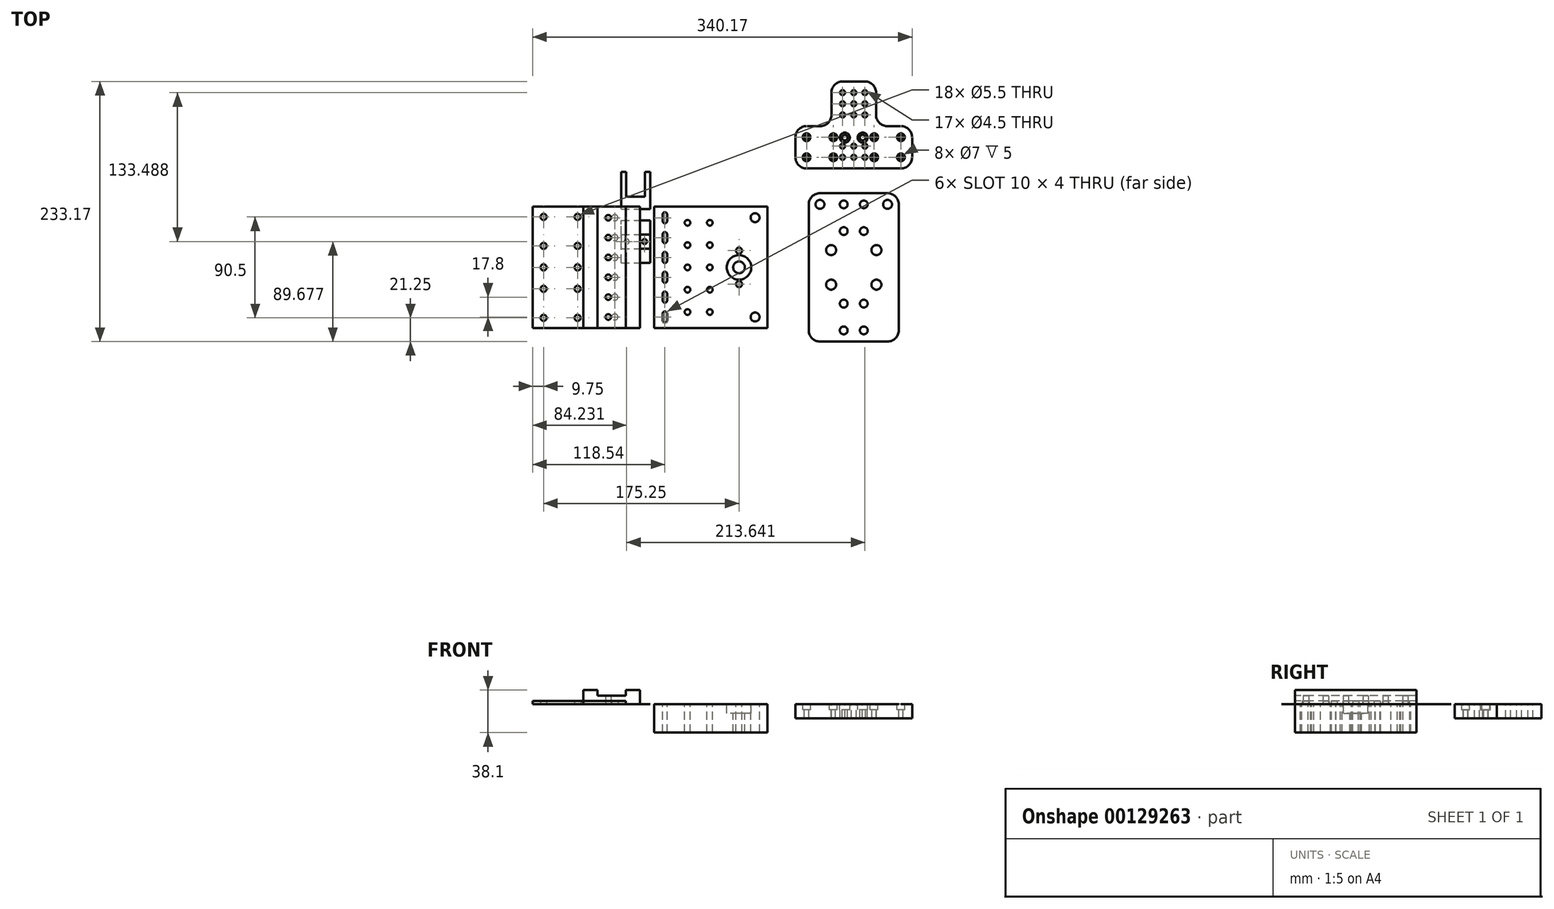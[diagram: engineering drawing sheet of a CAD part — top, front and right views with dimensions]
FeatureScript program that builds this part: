
annotation { "Feature Type Name" : "Feature", "Feature Type Description" : "" }
export const myFeature = defineFeature(function(context is Context, id is Id, definition is map)
    precondition{}
    {
        {
            var Q0;
            Q0=qCreatedBy(makeId("Top.planeOp"),FACE);
            var sketch = newSketch(context, id + "F0", { "sketchPlane" : qUnion([Q0])});
            skLineSegment(sketch, "E0.bottom", {"start": v(0, 0) * mm, "end": v(101.6, 0) * mm});
            skLineSegment(sketch, "E0.top", {"start": v(0, 109) * mm, "end": v(101.6, 109) * mm});
            skLineSegment(sketch, "E0.left", {"start": v(0, 0) * mm, "end": v(0, 109) * mm});
            skLineSegment(sketch, "E0.right", {"start": v(101.6, 0) * mm, "end": v(101.6, 109) * mm});
            skLineSegment(sketch, "E1", {"start": v(9.74, 0) * mm, "end": v(9.74, 109) * mm, "construction": true});
            skLineSegment(sketch, "E2", {"start": v(0, 10) * mm, "end": v(9.74, 10) * mm, "construction": true});
            skLineSegment(sketch, "E3.0.1.0", {"start": v(0, 27.8) * mm, "end": v(9.74, 27.8) * mm, "construction": true});
            skLineSegment(sketch, "E3.0.2.0", {"start": v(0, 45.6) * mm, "end": v(9.74, 45.6) * mm, "construction": true});
            skLineSegment(sketch, "E3.0.3.0", {"start": v(0, 63.4) * mm, "end": v(9.74, 63.4) * mm, "construction": true});
            skLineSegment(sketch, "E3.0.4.0", {"start": v(0, 81.2) * mm, "end": v(9.74, 81.2) * mm, "construction": true});
            skLineSegment(sketch, "E3.0.5.0", {"start": v(0, 99) * mm, "end": v(9.74, 99) * mm, "construction": true});
            skLineSegment(sketch, "E3.direction2", {"start": v(0, 10) * mm, "end": v(0, 27.8) * mm, "construction": true});
            skArc(sketch, "E4", {"start": v(11.74, 30.8) * mm, "mid": v(9.74, 32.8) * mm, "end": v(7.74, 30.8) * mm});
            skLineSegment(sketch, "E5", {"start": v(9.74, 30.8) * mm, "end": v(9.74, 24.8) * mm, "construction": true});
            skArc(sketch, "E6", {"start": v(7.74, 24.8) * mm, "mid": v(9.74, 22.8) * mm, "end": v(11.74, 24.8) * mm});
            skLineSegment(sketch, "E7", {"start": v(11.74, 30.8) * mm, "end": v(11.74, 24.8) * mm});
            skLineSegment(sketch, "E8", {"start": v(7.74, 24.8) * mm, "end": v(7.74, 30.8) * mm});
            skPoint(sketch, "E9", {"position": v(9.74, 27.8) * mm});
            skArc(sketch, "E10", {"start": v(11.74, 48.6) * mm, "mid": v(9.74, 50.6) * mm, "end": v(7.74, 48.6) * mm});
            skLineSegment(sketch, "E11", {"start": v(9.74, 48.6) * mm, "end": v(9.74, 42.6) * mm, "construction": true});
            skArc(sketch, "E12", {"start": v(7.74, 42.6) * mm, "mid": v(9.74, 40.6) * mm, "end": v(11.74, 42.6) * mm});
            skLineSegment(sketch, "E13", {"start": v(11.74, 48.6) * mm, "end": v(11.74, 42.6) * mm});
            skLineSegment(sketch, "E14", {"start": v(7.74, 42.6) * mm, "end": v(7.74, 48.6) * mm});
            skPoint(sketch, "E15", {"position": v(9.74, 45.6) * mm});
            skArc(sketch, "E16", {"start": v(11.74, 102) * mm, "mid": v(9.74, 104) * mm, "end": v(7.74, 102) * mm});
            skLineSegment(sketch, "E17", {"start": v(9.74, 102) * mm, "end": v(9.74, 96) * mm, "construction": true});
            skArc(sketch, "E18", {"start": v(7.74, 96) * mm, "mid": v(9.74, 94) * mm, "end": v(11.74, 96) * mm});
            skLineSegment(sketch, "E19", {"start": v(11.74, 102) * mm, "end": v(11.74, 96) * mm});
            skLineSegment(sketch, "E20", {"start": v(7.74, 96) * mm, "end": v(7.74, 102) * mm});
            skPoint(sketch, "E21", {"position": v(9.74, 99) * mm});
            skArc(sketch, "E22", {"start": v(11.74, 13) * mm, "mid": v(9.74, 15) * mm, "end": v(7.74, 13) * mm});
            skLineSegment(sketch, "E23", {"start": v(9.74, 13) * mm, "end": v(9.74, 7) * mm, "construction": true});
            skArc(sketch, "E24", {"start": v(7.74, 7) * mm, "mid": v(9.74, 5) * mm, "end": v(11.74, 7) * mm});
            skLineSegment(sketch, "E25", {"start": v(11.74, 13) * mm, "end": v(11.74, 7) * mm});
            skLineSegment(sketch, "E26", {"start": v(7.74, 7) * mm, "end": v(7.74, 13) * mm});
            skPoint(sketch, "E27", {"position": v(9.74, 10) * mm});
            skArc(sketch, "E28", {"start": v(11.74, 84.2) * mm, "mid": v(9.74, 86.2) * mm, "end": v(7.74, 84.2) * mm});
            skLineSegment(sketch, "E29", {"start": v(9.74, 84.2) * mm, "end": v(9.74, 78.2) * mm, "construction": true});
            skArc(sketch, "E30", {"start": v(7.74, 78.2) * mm, "mid": v(9.74, 76.2) * mm, "end": v(11.74, 78.2) * mm});
            skLineSegment(sketch, "E31", {"start": v(11.74, 84.2) * mm, "end": v(11.74, 78.2) * mm});
            skLineSegment(sketch, "E32", {"start": v(7.74, 78.2) * mm, "end": v(7.74, 84.2) * mm});
            skPoint(sketch, "E33", {"position": v(9.74, 81.2) * mm});
            skArc(sketch, "E34", {"start": v(11.74, 66.4) * mm, "mid": v(9.74, 68.4) * mm, "end": v(7.74, 66.4) * mm});
            skLineSegment(sketch, "E35", {"start": v(9.74, 66.4) * mm, "end": v(9.74, 60.4) * mm, "construction": true});
            skArc(sketch, "E36", {"start": v(7.74, 60.4) * mm, "mid": v(9.74, 58.4) * mm, "end": v(11.74, 60.4) * mm});
            skLineSegment(sketch, "E37", {"start": v(11.74, 66.4) * mm, "end": v(11.74, 60.4) * mm});
            skLineSegment(sketch, "E38", {"start": v(7.74, 60.4) * mm, "end": v(7.74, 66.4) * mm});
            skPoint(sketch, "E39", {"position": v(9.74, 63.4) * mm});
            skLineSegment(sketch, "E40", {"start": v(76.2, 109) * mm, "end": v(76.2, 0) * mm, "construction": true});
            skPoint(sketch, "E41", {"position": v(76.2, 69.5) * mm});
            skPoint(sketch, "E42", {"position": v(76.2, 54.5) * mm});
            skPoint(sketch, "E43", {"position": v(76.2, 39.5) * mm});
            skCircle(sketch, "E44", {"center": v(76.2, 69.5) * mm, "radius": 2.75 * mm});
            skCircle(sketch, "E45", {"center": v(76.2, 39.5) * mm, "radius": 2.75 * mm});
            skCircle(sketch, "E46", {"center": v(76.2, 54.5) * mm, "radius": 11 * mm});
            skCircle(sketch, "E47", {"center": v(76.2, 54.5) * mm, "radius": 5.26 * mm});
            skLineSegment(sketch, "E48", {"start": v(122.66, 27) * mm, "end": v(122.66, -7) * mm, "construction": true});
            skLineSegment(sketch, "E49", {"start": v(90.6, 10) * mm, "end": v(122.66, 10) * mm, "construction": true});
            skPoint(sketch, "E50", {"position": v(122.66, 10) * mm});
            skLineSegment(sketch, "E51", {"start": v(90.6, 99) * mm, "end": v(122.66, 99) * mm, "construction": true});
            skLineSegment(sketch, "E52", {"start": v(122.66, 116) * mm, "end": v(122.66, 82) * mm, "construction": true});
            skPoint(sketch, "E53", {"position": v(122.66, 99) * mm});
            skLineSegment(sketch, "E54", {"start": v(122.66, 54.5) * mm, "end": v(76.2, 54.5) * mm, "construction": true});
            skLineSegment(sketch, "E55", {"start": v(122.66, 74.5) * mm, "end": v(122.66, 34.5) * mm, "construction": true});
            skPoint(sketch, "E56", {"position": v(122.66, 54.5) * mm});
            skLineSegment(sketch, "E57", {"start": v(90.6, 109) * mm, "end": v(90.6, 0) * mm, "construction": true});
            skPoint(sketch, "E58", {"position": v(90.6, 99) * mm});
            skPoint(sketch, "E59", {"position": v(90.6, 10) * mm});
            skLineSegment(sketch, "E60", {"start": v(122.66, 82) * mm, "end": v(122.66, 74.5) * mm, "construction": true});
            skLineSegment(sketch, "E61", {"start": v(122.66, 34.5) * mm, "end": v(122.66, 27) * mm, "construction": true});
            skCircle(sketch, "E62", {"center": v(90.6, 99) * mm, "radius": 4 * mm});
            skCircle(sketch, "E63", {"center": v(90.6, 10) * mm, "radius": 4 * mm});
            skLineSegment(sketch, "E64", {"start": v(30, 109) * mm, "end": v(30, 0) * mm, "construction": true});
            skLineSegment(sketch, "E65", {"start": v(50, 109) * mm, "end": v(50, 0) * mm, "construction": true});
            skLineSegment(sketch, "E66", {"start": v(50, 54.5) * mm, "end": v(30, 54.5) * mm, "construction": true});
            skLineSegment(sketch, "E67", {"start": v(30, 74.5) * mm, "end": v(50, 74.5) * mm, "construction": true});
            skLineSegment(sketch, "E68", {"start": v(50, 94.5) * mm, "end": v(30, 94.5) * mm, "construction": true});
            skLineSegment(sketch, "E69", {"start": v(30, 34.5) * mm, "end": v(50, 34.5) * mm, "construction": true});
            skLineSegment(sketch, "E70", {"start": v(50, 14.5) * mm, "end": v(30, 14.5) * mm, "construction": true});
            skCircle(sketch, "E71", {"center": v(30, 94.5) * mm, "radius": 2.55 * mm});
            skCircle(sketch, "E72", {"center": v(50, 94.5) * mm, "radius": 2.55 * mm});
            skCircle(sketch, "E73", {"center": v(30, 74.5) * mm, "radius": 2.55 * mm});
            skCircle(sketch, "E74", {"center": v(50, 74.5) * mm, "radius": 2.55 * mm});
            skCircle(sketch, "E75", {"center": v(50, 54.5) * mm, "radius": 2.55 * mm});
            skCircle(sketch, "E76", {"center": v(30, 54.5) * mm, "radius": 2.55 * mm});
            skCircle(sketch, "E77", {"center": v(30, 34.5) * mm, "radius": 2.55 * mm});
            skCircle(sketch, "E78", {"center": v(50, 34.5) * mm, "radius": 2.55 * mm});
            skCircle(sketch, "E79", {"center": v(50, 14.5) * mm, "radius": 2.55 * mm});
            skCircle(sketch, "E80", {"center": v(30, 14.5) * mm, "radius": 2.55 * mm});
            skLineSegment(sketch, "E81", {"start": v(101.6, 116.15) * mm, "end": v(101.6, 102.86) * mm});
            skLineSegment(sketch, "E82", {"start": v(76.2, 85.11) * mm, "end": v(94.2, 85.11) * mm});
            skSolve(sketch);
        }
        {
            var Q0;
            Q0=qCreatedBy(makeId("Top.planeOp"),FACE);
            var sketch = newSketch(context, id + "F1", { "sketchPlane" : qUnion([Q0])});
            skLineSegment(sketch, "E83.bottom", {"start": v(-25.4, 0) * mm, "end": v(-50.8, 0) * mm});
            skLineSegment(sketch, "E83.top", {"start": v(-25.4, 109) * mm, "end": v(-50.8, 109) * mm});
            skLineSegment(sketch, "E83.left", {"start": v(-25.4, 0) * mm, "end": v(-25.4, 109) * mm, "construction": true});
            skLineSegment(sketch, "E83.right", {"start": v(-50.8, 0) * mm, "end": v(-50.8, 109) * mm, "construction": true});
            skLineSegment(sketch, "E84", {"start": v(0, 0) * mm, "end": v(-25.4, 0) * mm, "construction": true});
            skLineSegment(sketch, "E85", {"start": v(-25.4, 109) * mm, "end": v(0, 109) * mm, "construction": true});
            skLineSegment(sketch, "E86", {"start": v(-50.8, 99) * mm, "end": v(0, 99) * mm, "construction": true});
            skLineSegment(sketch, "E87", {"start": v(-50.8, 81.2) * mm, "end": v(0, 81.2) * mm, "construction": true});
            skLineSegment(sketch, "E88", {"start": v(-50.8, 63.4) * mm, "end": v(0, 63.4) * mm, "construction": true});
            skLineSegment(sketch, "E89", {"start": v(-50.8, 45.6) * mm, "end": v(0, 45.6) * mm, "construction": true});
            skLineSegment(sketch, "E90", {"start": v(-50.8, 27.8) * mm, "end": v(0, 27.8) * mm, "construction": true});
            skLineSegment(sketch, "E91", {"start": v(-50.8, 10) * mm, "end": v(0, 10) * mm, "construction": true});
            skLineSegment(sketch, "E92", {"start": v(-41.06, 109) * mm, "end": v(-41.06, 0) * mm, "construction": true});
            skCircle(sketch, "E93", {"center": v(-41.06, 99) * mm, "radius": 2.5 * mm});
            skCircle(sketch, "E94", {"center": v(-41.06, 81.2) * mm, "radius": 2.5 * mm});
            skCircle(sketch, "E95", {"center": v(-41.06, 63.4) * mm, "radius": 2.5 * mm});
            skCircle(sketch, "E96", {"center": v(-41.06, 45.6) * mm, "radius": 2.5 * mm});
            skCircle(sketch, "E97", {"center": v(-41.06, 27.8) * mm, "radius": 2.5 * mm});
            skCircle(sketch, "E98", {"center": v(-41.06, 10) * mm, "radius": 2.5 * mm});
            skLineSegment(sketch, "E99", {"start": v(-50.8, 109) * mm, "end": v(-63.5, 109) * mm});
            skLineSegment(sketch, "E100", {"start": v(-63.5, 109) * mm, "end": v(-63.5, 0) * mm});
            skLineSegment(sketch, "E101", {"start": v(-63.5, 0) * mm, "end": v(-50.8, 0) * mm});
            skLineSegment(sketch, "E102", {"start": v(-25.4, 0) * mm, "end": v(-12.7, 0) * mm});
            skPoint(sketch, "E102.endSnap0", {"position": v(-12.7, 0) * mm});
            skLineSegment(sketch, "E103", {"start": v(-12.7, 0) * mm, "end": v(-12.7, 109) * mm});
            skLineSegment(sketch, "E104", {"start": v(-12.7, 109) * mm, "end": v(-25.4, 109) * mm});
            skSolve(sketch);
        }
        {
            var Q0;
            Q0=makeQuery(id+"F1.imprint","IMPRINT",FACE,{"disambiguationData":[TD([[makeQuery(id+"F1.imprint","IMPRINT",EDGE,{"derivedFrom":sQuery(id+"F1.wireOp",EDGE,"E83.bottom")}),-1.0]])]});
            extrude(context, id + "F2", {"entities" : qUnion([Q0]), "depth" : 12.7 * mm});
        }
        {
            var Q0;
            Q0=makeQuery(id+"F2.opExtrude","CAP_FACE",FACE,{"disambiguationData":[OSD([sQuery(id+"F1.wireOp",EDGE,"E83.bottom"),sQuery(id+"F1.wireOp",EDGE,"E83.top"),sQuery(id+"F1.wireOp",EDGE,"E93"),sQuery(id+"F1.wireOp",EDGE,"E94"),sQuery(id+"F1.wireOp",EDGE,"E95"),sQuery(id+"F1.wireOp",EDGE,"E96"),sQuery(id+"F1.wireOp",EDGE,"E97"),sQuery(id+"F1.wireOp",EDGE,"E98"),sQuery(id+"F1.wireOp",EDGE,"E99"),sQuery(id+"F1.wireOp",EDGE,"E100"),sQuery(id+"F1.wireOp",EDGE,"E101"),sQuery(id+"F1.wireOp",EDGE,"E102"),sQuery(id+"F1.wireOp",EDGE,"E103"),sQuery(id+"F1.wireOp",EDGE,"E104")])],"isStart":false});
            var sketch = newSketch(context, id + "F3", { "sketchPlane" : qUnion([Q0])});
            skLineSegment(sketch, "E105", {"start": v(-50.8, 109) * mm, "end": v(-50.8, 0) * mm});
            skLineSegment(sketch, "E106", {"start": v(-25.4, 109) * mm, "end": v(-25.4, 0) * mm});
            skSolve(sketch);
        }
        {
            var Q0;
            {var subQ0=sQuery(id+"F3.wireOp",EDGE,"E105");Q0=makeQuery(id+"F3.imprint","IMPRINT",FACE,{"disambiguationData":[TD([[makeQuery(id+"F3.imprint","IMPRINT",EDGE,{"derivedFrom":subQ0}),1.0]])]});}
            extrude(context, id + "F4", {"entities" : qUnion([Q0]), "operationType" : NewBodyOperationType.REMOVE, "oppositeDirection" : true, "depth" : 5 * mm});
        }
        {
            var Q0;
            Q0=makeQuery(id+"F0.imprint","IMPRINT",FACE,{"disambiguationData":[TD([[makeQuery(id+"F0.imprint","IMPRINT",EDGE,{"derivedFrom":sQuery(id+"F0.wireOp",EDGE,"E46")}),1.0]])]});
            var Q1;
            Q1=makeQuery(id+"F0.imprint","IMPRINT",FACE,{"disambiguationData":[TD([[makeQuery(id+"F0.imprint","IMPRINT",EDGE,{"derivedFrom":sQuery(id+"F0.wireOp",EDGE,"E0.bottom")}),1.0]])]});
            extrude(context, id + "F5", {"entities" : qUnion([Q0, Q1]), "oppositeDirection" : true, "depth" : 25.4 * mm});
        }
        {
            var Q0;
            Q0=makeQuery(id+"F0.imprint","IMPRINT",FACE,{"disambiguationData":[TD([[makeQuery(id+"F0.imprint","IMPRINT",EDGE,{"derivedFrom":sQuery(id+"F0.wireOp",EDGE,"E46")}),1.0]])]});
            extrude(context, id + "F6", {"entities" : qUnion([Q0]), "operationType" : NewBodyOperationType.REMOVE, "oppositeDirection" : true, "depth" : 8 * mm});
        }
        {
            var Q0;
            Q0=makeQuery(id+"F0.imprint","IMPRINT",FACE,{"disambiguationData":[TD([[makeQuery(id+"F0.imprint","IMPRINT",EDGE,{"derivedFrom":sQuery(id+"F0.wireOp",EDGE,"E0.bottom")}),1.0]])]});
            var sketch = newSketch(context, id + "F7", { "sketchPlane" : qUnion([Q0])});
            skLineSegment(sketch, "E107.bottom", {"start": v(-25.4, 109) * mm, "end": v(-58.8, 109) * mm});
            skLineSegment(sketch, "E107.top", {"start": v(-25.4, 0) * mm, "end": v(-108.8, 0) * mm});
            skLineSegment(sketch, "E107.left", {"start": v(-25.4, 109) * mm, "end": v(-25.4, 0) * mm});
            skLineSegment(sketch, "E107.right", {"start": v(-108.8, 109) * mm, "end": v(-108.8, 0) * mm});
            skLineSegment(sketch, "E108", {"start": v(0, 109) * mm, "end": v(-25.4, 109) * mm, "construction": true});
            skLineSegment(sketch, "E109", {"start": v(0, 0) * mm, "end": v(-25.4, 0) * mm, "construction": true});
            skLineSegment(sketch, "E110", {"start": v(-58.8, 109) * mm, "end": v(-58.8, 54.5) * mm, "construction": true});
            skLineSegment(sketch, "E111", {"start": v(-35.14, 109) * mm, "end": v(-35.14, 0) * mm, "construction": true});
            skLineSegment(sketch, "E112", {"start": v(-35.14, 99) * mm, "end": v(0, 99) * mm, "construction": true});
            skLineSegment(sketch, "E113", {"start": v(-35.14, 81.2) * mm, "end": v(0, 81.2) * mm, "construction": true});
            skLineSegment(sketch, "E114", {"start": v(-35.14, 63.4) * mm, "end": v(0, 63.4) * mm, "construction": true});
            skLineSegment(sketch, "E115", {"start": v(-35.14, 45.6) * mm, "end": v(0, 45.6) * mm, "construction": true});
            skLineSegment(sketch, "E116", {"start": v(-35.14, 27.8) * mm, "end": v(0, 27.8) * mm, "construction": true});
            skLineSegment(sketch, "E117", {"start": v(-35.14, 10) * mm, "end": v(0, 10) * mm, "construction": true});
            skPoint(sketch, "E118", {"position": v(9.74, 109) * mm});
            skLineSegment(sketch, "E119", {"start": v(0, 109) * mm, "end": v(9.74, 109) * mm, "construction": true});
            skLineSegment(sketch, "E120", {"start": v(-25.4, 109) * mm, "end": v(-35.14, 109) * mm, "construction": true});
            skCircle(sketch, "E121", {"center": v(-35.14, 99) * mm, "radius": 2.75 * mm});
            skCircle(sketch, "E122", {"center": v(-35.14, 81.2) * mm, "radius": 2.75 * mm});
            skCircle(sketch, "E123", {"center": v(-35.14, 63.4) * mm, "radius": 2.75 * mm});
            skCircle(sketch, "E124", {"center": v(-35.14, 45.6) * mm, "radius": 2.75 * mm});
            skCircle(sketch, "E125", {"center": v(-35.14, 27.8) * mm, "radius": 2.75 * mm});
            skCircle(sketch, "E126", {"center": v(-35.14, 10) * mm, "radius": 2.75 * mm});
            skLineSegment(sketch, "E127", {"start": v(-58.8, 54.5) * mm, "end": v(-108.8, 54.5) * mm, "construction": true});
            skLineSegment(sketch, "E128", {"start": v(-58.8, 109) * mm, "end": v(-83.8, 109) * mm});
            skLineSegment(sketch, "E129", {"start": v(-58.8, 54.5) * mm, "end": v(-58.8, 0) * mm, "construction": true});
            skLineSegment(sketch, "E130", {"start": v(-83.8, 109) * mm, "end": v(-83.8, 0) * mm, "construction": true});
            skLineSegment(sketch, "E131", {"start": v(-99.05, 109) * mm, "end": v(-99.05, 0) * mm, "construction": true});
            skLineSegment(sketch, "E132", {"start": v(-68.55, 109) * mm, "end": v(-68.55, 0) * mm, "construction": true});
            skLineSegment(sketch, "E133", {"start": v(-83.8, 109) * mm, "end": v(-108.8, 109) * mm});
            skLineSegment(sketch, "E134", {"start": v(-50.8, 109) * mm, "end": v(-50.8, 0) * mm, "construction": true});
            skLineSegment(sketch, "E135", {"start": v(-108.8, 64.5) * mm, "end": v(-58.8, 64.5) * mm, "construction": true});
            skLineSegment(sketch, "E136", {"start": v(-108.8, 44.5) * mm, "end": v(-58.8, 44.5) * mm, "construction": true});
            skLineSegment(sketch, "E137", {"start": v(-108.8, 86.75) * mm, "end": v(-58.8, 86.75) * mm, "construction": true});
            skLineSegment(sketch, "E138", {"start": v(-108.8, 99.75) * mm, "end": v(-58.8, 99.75) * mm, "construction": true});
            skLineSegment(sketch, "E139", {"start": v(-108.8, 73.75) * mm, "end": v(-58.8, 73.75) * mm, "construction": true});
            skLineSegment(sketch, "E140", {"start": v(-108.8, 22.25) * mm, "end": v(-58.8, 22.25) * mm, "construction": true});
            skLineSegment(sketch, "E141", {"start": v(-108.8, 35.25) * mm, "end": v(-58.8, 35.25) * mm, "construction": true});
            skLineSegment(sketch, "E142", {"start": v(-58.8, 9.25) * mm, "end": v(-108.8, 9.25) * mm, "construction": true});
            skCircle(sketch, "E143", {"center": v(-99.05, 99.75) * mm, "radius": 2.75 * mm});
            skCircle(sketch, "E144", {"center": v(-68.55, 99.75) * mm, "radius": 2.75 * mm});
            skCircle(sketch, "E145", {"center": v(-68.55, 73.75) * mm, "radius": 2.75 * mm});
            skCircle(sketch, "E146", {"center": v(-99.05, 73.75) * mm, "radius": 2.75 * mm});
            skCircle(sketch, "E147", {"center": v(-99.05, 35.25) * mm, "radius": 2.75 * mm});
            skCircle(sketch, "E148", {"center": v(-99.05, 9.25) * mm, "radius": 2.75 * mm});
            skCircle(sketch, "E149", {"center": v(-68.55, 9.25) * mm, "radius": 2.75 * mm});
            skCircle(sketch, "E150", {"center": v(-68.55, 35.25) * mm, "radius": 2.75 * mm});
            skCircle(sketch, "E151", {"center": v(-68.55, 54.5) * mm, "radius": 2.75 * mm});
            skCircle(sketch, "E152", {"center": v(-99.05, 54.5) * mm, "radius": 2.75 * mm});
            skSolve(sketch);
        }
        {
            var Q0;
            Q0=makeQuery(id+"F7.imprint","IMPRINT",FACE,{"disambiguationData":[TD([[makeQuery(id+"F7.imprint","IMPRINT",EDGE,{"derivedFrom":sQuery(id+"F7.wireOp",EDGE,"E107.bottom")}),1.0]])]});
            extrude(context, id + "F8", {"entities" : qUnion([Q0]), "depth" : 3 * mm});
        }
        {
            var Q0;
            Q0=makeQuery(id+"F0.imprint","IMPRINT",FACE,{"disambiguationData":[TD([[makeQuery(id+"F0.imprint","IMPRINT",EDGE,{"derivedFrom":sQuery(id+"F0.wireOp",EDGE,"E0.bottom")}),1.0]])]});
            var sketch = newSketch(context, id + "F9", { "sketchPlane" : qUnion([Q0])});
            skLineSegment(sketch, "E153.bottom", {"start": v(148.77, -12) * mm, "end": v(209.37, -12) * mm});
            skLineSegment(sketch, "E153.top", {"start": v(148.77, 121) * mm, "end": v(209.37, 121) * mm});
            skLineSegment(sketch, "E153.left", {"start": v(209.37, 121) * mm, "end": v(209.37, -12) * mm, "construction": true});
            skLineSegment(sketch, "E153.right", {"start": v(148.77, 121) * mm, "end": v(148.77, -12) * mm, "construction": true});
            skLineSegment(sketch, "E154", {"start": v(148.77, 10) * mm, "end": v(122.66, 10) * mm, "construction": true});
            skLineSegment(sketch, "E155", {"start": v(148.77, 99) * mm, "end": v(122.66, 99) * mm, "construction": true});
            skLineSegment(sketch, "E156", {"start": v(179.07, 121) * mm, "end": v(179.07, -12) * mm, "construction": true});
            skLineSegment(sketch, "E157", {"start": v(122.66, 54.5) * mm, "end": v(148.77, 54.5) * mm, "construction": true});
            skLineSegment(sketch, "E158", {"start": v(188.07, 111) * mm, "end": v(188.07, 87) * mm, "construction": true});
            skPoint(sketch, "E159", {"position": v(188.07, 99) * mm});
            skLineSegment(sketch, "E160", {"start": v(188.07, 87) * mm, "end": v(170.07, 87) * mm, "construction": true});
            skPoint(sketch, "E161", {"position": v(179.07, 87) * mm});
            skLineSegment(sketch, "E162", {"start": v(188.07, 111) * mm, "end": v(170.07, 111) * mm, "construction": true});
            skLineSegment(sketch, "E163", {"start": v(170.07, 87) * mm, "end": v(170.07, 111) * mm, "construction": true});
            skLineSegment(sketch, "E164", {"start": v(188.07, 22) * mm, "end": v(188.07, -2) * mm, "construction": true});
            skPoint(sketch, "E165", {"position": v(188.07, 10) * mm});
            skLineSegment(sketch, "E166", {"start": v(188.07, 22) * mm, "end": v(170.07, 22) * mm, "construction": true});
            skPoint(sketch, "E167", {"position": v(179.07, 22) * mm});
            skLineSegment(sketch, "E168", {"start": v(170.07, 22) * mm, "end": v(170.07, -2) * mm, "construction": true});
            skLineSegment(sketch, "E169", {"start": v(170.07, -2) * mm, "end": v(188.07, -2) * mm, "construction": true});
            skLineSegment(sketch, "E170", {"start": v(199.37, 39) * mm, "end": v(158.77, 39) * mm, "construction": true});
            skPoint(sketch, "E171", {"position": v(179.07, 39) * mm});
            skLineSegment(sketch, "E172", {"start": v(158.77, 39) * mm, "end": v(158.77, 70) * mm, "construction": true});
            skLineSegment(sketch, "E173", {"start": v(158.77, 70) * mm, "end": v(199.37, 70) * mm, "construction": true});
            skCircle(sketch, "E174", {"center": v(170.07, 111) * mm, "radius": 2.25 * mm});
            skCircle(sketch, "E175", {"center": v(188.07, 87) * mm, "radius": 2.25 * mm});
            skCircle(sketch, "E176", {"center": v(170.07, 87) * mm, "radius": 2.25 * mm});
            skCircle(sketch, "E177", {"center": v(188.07, 111) * mm, "radius": 2.25 * mm});
            skCircle(sketch, "E178", {"center": v(188.07, 22) * mm, "radius": 2.25 * mm});
            skCircle(sketch, "E179", {"center": v(188.07, -2) * mm, "radius": 2.25 * mm});
            skCircle(sketch, "E180", {"center": v(170.07, 22) * mm, "radius": 2.25 * mm});
            skCircle(sketch, "E181", {"center": v(170.07, -2) * mm, "radius": 2.25 * mm});
            skCircle(sketch, "E182", {"center": v(158.77, 39) * mm, "radius": 2.75 * mm});
            skCircle(sketch, "E183", {"center": v(199.37, 70) * mm, "radius": 2.75 * mm});
            skCircle(sketch, "E184", {"center": v(158.77, 70) * mm, "radius": 2.75 * mm});
            skCircle(sketch, "E185", {"center": v(199.37, 39) * mm, "radius": 2.75 * mm});
            skLineSegment(sketch, "E186", {"start": v(170.07, 121) * mm, "end": v(170.07, -2) * mm, "construction": true});
            skLineSegment(sketch, "E187", {"start": v(199.37, 39) * mm, "end": v(199.37, 70) * mm, "construction": true});
            skPoint(sketch, "E188", {"position": v(158.77, 54.5) * mm});
            skLineSegment(sketch, "E189", {"start": v(158.77, 54.5) * mm, "end": v(148.77, 54.5) * mm, "construction": true});
            skLineSegment(sketch, "E190", {"start": v(148.77, 121) * mm, "end": v(148.77, 121) * mm});
            skLineSegment(sketch, "E191", {"start": v(138.77, 111) * mm, "end": v(138.77, -2) * mm});
            skLineSegment(sketch, "E192", {"start": v(148.77, -12) * mm, "end": v(148.77, -12) * mm});
            skLineSegment(sketch, "E193", {"start": v(209.37, -12) * mm, "end": v(209.37, -12) * mm});
            skLineSegment(sketch, "E194", {"start": v(219.37, -2) * mm, "end": v(219.37, 111) * mm});
            skLineSegment(sketch, "E195", {"start": v(209.37, 121) * mm, "end": v(209.37, 121) * mm});
            skPoint(sketch, "E196.visualSharp", {"position": v(138.77, 121) * mm});
            skArc(sketch, "E196.filletArc", {"start": v(148.77, 121) * mm, "mid": v(141.7, 118.07) * mm, "end": v(138.77, 111) * mm});
            skPoint(sketch, "E197.visualSharp", {"position": v(138.77, -12) * mm});
            skArc(sketch, "E197.filletArc", {"start": v(138.77, -2) * mm, "mid": v(141.7, -9.07) * mm, "end": v(148.77, -12) * mm});
            skCircle(sketch, "E198", {"center": v(148.77, 111) * mm, "radius": 4 * mm});
            skPoint(sketch, "E199.visualSharp", {"position": v(219.37, 121) * mm});
            skArc(sketch, "E199.filletArc", {"start": v(219.37, 111) * mm, "mid": v(216.44, 118.07) * mm, "end": v(209.37, 121) * mm});
            skPoint(sketch, "E200.visualSharp", {"position": v(219.37, -12) * mm});
            skArc(sketch, "E200.filletArc", {"start": v(209.37, -12) * mm, "mid": v(216.44, -9.07) * mm, "end": v(219.37, -2) * mm});
            skCircle(sketch, "E201", {"center": v(209.37, 111) * mm, "radius": 4 * mm});
            skCircle(sketch, "E202", {"center": v(158.77, 70) * mm, "radius": 4.5 * mm});
            skCircle(sketch, "E203", {"center": v(199.37, 70) * mm, "radius": 4.5 * mm});
            skCircle(sketch, "E204", {"center": v(158.77, 39) * mm, "radius": 4.5 * mm});
            skCircle(sketch, "E205", {"center": v(199.37, 39) * mm, "radius": 4.5 * mm});
            skCircle(sketch, "E206", {"center": v(170.07, 111) * mm, "radius": 3.5 * mm});
            skCircle(sketch, "E207", {"center": v(170.07, 87) * mm, "radius": 3.5 * mm});
            skCircle(sketch, "E208", {"center": v(188.07, 111) * mm, "radius": 3.5 * mm});
            skCircle(sketch, "E209", {"center": v(188.07, 87) * mm, "radius": 3.5 * mm});
            skCircle(sketch, "E210", {"center": v(170.07, 22) * mm, "radius": 3.5 * mm});
            skCircle(sketch, "E211", {"center": v(170.07, -2) * mm, "radius": 3.5 * mm});
            skCircle(sketch, "E212", {"center": v(188.07, 22) * mm, "radius": 3.5 * mm});
            skCircle(sketch, "E213", {"center": v(188.07, -2) * mm, "radius": 3.5 * mm});
            skSolve(sketch);
        }
        {
            var Q0;
            Q0=makeQuery(id+"F9.imprint","IMPRINT",FACE,{"disambiguationData":[TD([[makeQuery(id+"F9.imprint","IMPRINT",EDGE,{"derivedFrom":sQuery(id+"F9.wireOp",EDGE,"E153.bottom")}),-1.0]])]});
            var Q1;
            Q1=makeQuery(id+"F9.imprint","IMPRINT",FACE,{"disambiguationData":[TD([[makeQuery(id+"F9.imprint","IMPRINT",EDGE,{"derivedFrom":sQuery(id+"F9.wireOp",EDGE,"E153.bottom")}),1.0]])]});
            var Q2;
            Q2=makeQuery(id+"F9.imprint","IMPRINT",FACE,{"disambiguationData":[TD([[makeQuery(id+"F9.imprint","IMPRINT",EDGE,{"derivedFrom":sQuery(id+"F9.wireOp",EDGE,"E174")}),-1.0]])]});
            var Q3;
            Q3=makeQuery(id+"F9.imprint","IMPRINT",FACE,{"disambiguationData":[TD([[makeQuery(id+"F9.imprint","IMPRINT",EDGE,{"derivedFrom":sQuery(id+"F9.wireOp",EDGE,"E176")}),-1.0]])]});
            var Q4;
            Q4=makeQuery(id+"F9.imprint","IMPRINT",FACE,{"disambiguationData":[TD([[makeQuery(id+"F9.imprint","IMPRINT",EDGE,{"derivedFrom":sQuery(id+"F9.wireOp",EDGE,"E175")}),-1.0]])]});
            var Q5;
            Q5=makeQuery(id+"F9.imprint","IMPRINT",FACE,{"disambiguationData":[TD([[makeQuery(id+"F9.imprint","IMPRINT",EDGE,{"derivedFrom":sQuery(id+"F9.wireOp",EDGE,"E177")}),-1.0]])]});
            var Q6;
            Q6=makeQuery(id+"F9.imprint","IMPRINT",FACE,{"disambiguationData":[TD([[makeQuery(id+"F9.imprint","IMPRINT",EDGE,{"derivedFrom":sQuery(id+"F9.wireOp",EDGE,"E184")}),-1.0]])]});
            var Q7;
            Q7=makeQuery(id+"F9.imprint","IMPRINT",FACE,{"disambiguationData":[TD([[makeQuery(id+"F9.imprint","IMPRINT",EDGE,{"derivedFrom":sQuery(id+"F9.wireOp",EDGE,"E182")}),-1.0]])]});
            var Q8;
            Q8=makeQuery(id+"F9.imprint","IMPRINT",FACE,{"disambiguationData":[TD([[makeQuery(id+"F9.imprint","IMPRINT",EDGE,{"derivedFrom":sQuery(id+"F9.wireOp",EDGE,"E185")}),-1.0]])]});
            var Q9;
            Q9=makeQuery(id+"F9.imprint","IMPRINT",FACE,{"disambiguationData":[TD([[makeQuery(id+"F9.imprint","IMPRINT",EDGE,{"derivedFrom":sQuery(id+"F9.wireOp",EDGE,"E183")}),-1.0]])]});
            var Q10;
            Q10=makeQuery(id+"F9.imprint","IMPRINT",FACE,{"disambiguationData":[TD([[makeQuery(id+"F9.imprint","IMPRINT",EDGE,{"derivedFrom":sQuery(id+"F9.wireOp",EDGE,"E180")}),-1.0]])]});
            var Q11;
            Q11=makeQuery(id+"F9.imprint","IMPRINT",FACE,{"disambiguationData":[TD([[makeQuery(id+"F9.imprint","IMPRINT",EDGE,{"derivedFrom":sQuery(id+"F9.wireOp",EDGE,"E181")}),-1.0]])]});
            var Q12;
            Q12=makeQuery(id+"F9.imprint","IMPRINT",FACE,{"disambiguationData":[TD([[makeQuery(id+"F9.imprint","IMPRINT",EDGE,{"derivedFrom":sQuery(id+"F9.wireOp",EDGE,"E179")}),-1.0]])]});
            var Q13;
            Q13=makeQuery(id+"F9.imprint","IMPRINT",FACE,{"disambiguationData":[TD([[makeQuery(id+"F9.imprint","IMPRINT",EDGE,{"derivedFrom":sQuery(id+"F9.wireOp",EDGE,"E178")}),-1.0]])]});
            extrude(context, id + "F10", {"entities" : qUnion([Q0, Q1, Q2, Q3, Q4, Q5, Q6, Q7, Q8, Q9, Q10, Q11, Q12, Q13]), "oppositeDirection" : true, "depth" : 1 / 50.8 * mm});
        }
        {
            var Q0;
            Q0=makeQuery(id+"F9.imprint","IMPRINT",FACE,{"disambiguationData":[TD([[makeQuery(id+"F9.imprint","IMPRINT",EDGE,{"derivedFrom":sQuery(id+"F9.wireOp",EDGE,"E184")}),-1.0]])]});
            var Q1;
            Q1=makeQuery(id+"F9.imprint","IMPRINT",FACE,{"disambiguationData":[TD([[makeQuery(id+"F9.imprint","IMPRINT",EDGE,{"derivedFrom":sQuery(id+"F9.wireOp",EDGE,"E174")}),-1.0]])]});
            var Q2;
            Q2=makeQuery(id+"F9.imprint","IMPRINT",FACE,{"disambiguationData":[TD([[makeQuery(id+"F9.imprint","IMPRINT",EDGE,{"derivedFrom":sQuery(id+"F9.wireOp",EDGE,"E177")}),-1.0]])]});
            var Q3;
            Q3=makeQuery(id+"F9.imprint","IMPRINT",FACE,{"disambiguationData":[TD([[makeQuery(id+"F9.imprint","IMPRINT",EDGE,{"derivedFrom":sQuery(id+"F9.wireOp",EDGE,"E175")}),-1.0]])]});
            var Q4;
            Q4=makeQuery(id+"F9.imprint","IMPRINT",FACE,{"disambiguationData":[TD([[makeQuery(id+"F9.imprint","IMPRINT",EDGE,{"derivedFrom":sQuery(id+"F9.wireOp",EDGE,"E176")}),-1.0]])]});
            var Q5;
            Q5=makeQuery(id+"F9.imprint","IMPRINT",FACE,{"disambiguationData":[TD([[makeQuery(id+"F9.imprint","IMPRINT",EDGE,{"derivedFrom":sQuery(id+"F9.wireOp",EDGE,"E183")}),-1.0]])]});
            var Q6;
            Q6=makeQuery(id+"F9.imprint","IMPRINT",FACE,{"disambiguationData":[TD([[makeQuery(id+"F9.imprint","IMPRINT",EDGE,{"derivedFrom":sQuery(id+"F9.wireOp",EDGE,"E182")}),-1.0]])]});
            var Q7;
            Q7=makeQuery(id+"F9.imprint","IMPRINT",FACE,{"disambiguationData":[TD([[makeQuery(id+"F9.imprint","IMPRINT",EDGE,{"derivedFrom":sQuery(id+"F9.wireOp",EDGE,"E185")}),-1.0]])]});
            var Q8;
            Q8=makeQuery(id+"F9.imprint","IMPRINT",FACE,{"disambiguationData":[TD([[makeQuery(id+"F9.imprint","IMPRINT",EDGE,{"derivedFrom":sQuery(id+"F9.wireOp",EDGE,"E178")}),-1.0]])]});
            var Q9;
            Q9=makeQuery(id+"F9.imprint","IMPRINT",FACE,{"disambiguationData":[TD([[makeQuery(id+"F9.imprint","IMPRINT",EDGE,{"derivedFrom":sQuery(id+"F9.wireOp",EDGE,"E180")}),-1.0]])]});
            var Q10;
            Q10=makeQuery(id+"F9.imprint","IMPRINT",FACE,{"disambiguationData":[TD([[makeQuery(id+"F9.imprint","IMPRINT",EDGE,{"derivedFrom":sQuery(id+"F9.wireOp",EDGE,"E179")}),-1.0]])]});
            var Q11;
            Q11=makeQuery(id+"F9.imprint","IMPRINT",FACE,{"disambiguationData":[TD([[makeQuery(id+"F9.imprint","IMPRINT",EDGE,{"derivedFrom":sQuery(id+"F9.wireOp",EDGE,"E181")}),-1.0]])]});
            extrude(context, id + "F11", {"entities" : qUnion([Q0, Q1, Q2, Q3, Q4, Q5, Q6, Q7, Q8, Q9, Q10, Q11]), "operationType" : NewBodyOperationType.REMOVE, "oppositeDirection" : true, "depth" : 5 * mm});
        }
        {
            var Q0;
            Q0=makeQuery(id+"F9.imprint","IMPRINT",FACE,{"disambiguationData":[TD([[makeQuery(id+"F9.imprint","IMPRINT",EDGE,{"derivedFrom":sQuery(id+"F9.wireOp",EDGE,"E153.bottom")}),1.0]])]});
            var sketch = newSketch(context, id + "F12", { "sketchPlane" : qUnion([Q0])});
            skLineSegment(sketch, "E214", {"start": v(148.77, 162.17) * mm, "end": v(148.77, 111) * mm, "construction": true});
            skLineSegment(sketch, "E215", {"start": v(209.37, 162.17) * mm, "end": v(209.37, 111) * mm, "construction": true});
            skLineSegment(sketch, "E216", {"start": v(209.37, 162.17) * mm, "end": v(148.77, 162.17) * mm, "construction": true});
            skLineSegment(sketch, "E217.bottom", {"start": v(160.77, 153.17) * mm, "end": v(136.77, 153.17) * mm, "construction": true});
            skLineSegment(sketch, "E217.top", {"start": v(160.77, 171.17) * mm, "end": v(136.77, 171.17) * mm, "construction": true});
            skLineSegment(sketch, "E217.left", {"start": v(160.77, 153.17) * mm, "end": v(160.77, 171.17) * mm, "construction": true});
            skLineSegment(sketch, "E217.right", {"start": v(136.77, 153.17) * mm, "end": v(136.77, 171.17) * mm, "construction": true});
            skPoint(sketch, "E217.middle", {"position": v(148.77, 162.17) * mm});
            skLineSegment(sketch, "E218.bottom", {"start": v(221.37, 153.17) * mm, "end": v(197.37, 153.17) * mm, "construction": true});
            skLineSegment(sketch, "E218.top", {"start": v(221.37, 171.17) * mm, "end": v(197.37, 171.17) * mm, "construction": true});
            skLineSegment(sketch, "E218.left", {"start": v(221.37, 153.17) * mm, "end": v(221.37, 171.17) * mm, "construction": true});
            skLineSegment(sketch, "E218.right", {"start": v(197.37, 153.17) * mm, "end": v(197.37, 171.17) * mm, "construction": true});
            skPoint(sketch, "E218.middle", {"position": v(209.37, 162.17) * mm});
            skLineSegment(sketch, "E219.bottom", {"start": v(231.37, 181.17) * mm, "end": v(126.77, 181.17) * mm, "construction": true});
            skLineSegment(sketch, "E219.top", {"start": v(221.37, 143.17) * mm, "end": v(136.77, 143.17) * mm});
            skLineSegment(sketch, "E219.left", {"start": v(231.37, 171.17) * mm, "end": v(231.37, 153.17) * mm});
            skLineSegment(sketch, "E219.right", {"start": v(126.77, 171.17) * mm, "end": v(126.77, 153.17) * mm});
            skPoint(sketch, "E219.middle", {"position": v(179.07, 162.17) * mm});
            skCircle(sketch, "E220", {"center": v(136.77, 171.17) * mm, "radius": 2 * mm});
            skCircle(sketch, "E221", {"center": v(136.77, 153.17) * mm, "radius": 2 * mm});
            skCircle(sketch, "E222", {"center": v(160.77, 171.17) * mm, "radius": 2 * mm});
            skCircle(sketch, "E223", {"center": v(160.77, 153.17) * mm, "radius": 2 * mm});
            skCircle(sketch, "E224", {"center": v(197.37, 153.17) * mm, "radius": 2 * mm});
            skCircle(sketch, "E225", {"center": v(197.37, 171.17) * mm, "radius": 2 * mm});
            skCircle(sketch, "E226", {"center": v(221.37, 171.17) * mm, "radius": 2 * mm});
            skCircle(sketch, "E227", {"center": v(221.37, 153.17) * mm, "radius": 2 * mm});
            skLineSegment(sketch, "E228", {"start": v(169.07, 221.17) * mm, "end": v(189.07, 221.17) * mm});
            skLineSegment(sketch, "E229", {"start": v(126.77, 177.17) * mm, "end": v(231.37, 177.17) * mm, "construction": true});
            skLineSegment(sketch, "E230", {"start": v(126.77, 164.47) * mm, "end": v(231.37, 164.47) * mm, "construction": true});
            skLineSegment(sketch, "E231", {"start": v(179.07, 177.17) * mm, "end": v(179.07, 164.47) * mm, "construction": true});
            skLineSegment(sketch, "E232", {"start": v(179.07, 170.82) * mm, "end": v(187.07, 170.82) * mm, "construction": true});
            skLineSegment(sketch, "E233", {"start": v(179.07, 170.82) * mm, "end": v(171.07, 170.82) * mm, "construction": true});
            skCircle(sketch, "E234", {"center": v(187.07, 170.82) * mm, "radius": 2.5 * mm});
            skCircle(sketch, "E235", {"center": v(171.07, 170.82) * mm, "radius": 2.5 * mm});
            skCircle(sketch, "E236", {"center": v(171.07, 170.82) * mm, "radius": 4.5 * mm});
            skCircle(sketch, "E237", {"center": v(187.07, 170.82) * mm, "radius": 4.5 * mm});
            skLineSegment(sketch, "E238", {"start": v(179.07, 143.17) * mm, "end": v(179.07, 221.17) * mm, "construction": true});
            skLineSegment(sketch, "E239", {"start": v(169.07, 221.17) * mm, "end": v(169.07, 143.17) * mm, "construction": true});
            skLineSegment(sketch, "E240", {"start": v(189.07, 221.17) * mm, "end": v(189.07, 143.17) * mm, "construction": true});
            skLineSegment(sketch, "E241", {"start": v(169.07, 211.17) * mm, "end": v(189.07, 211.17) * mm, "construction": true});
            skLineSegment(sketch, "E242", {"start": v(169.07, 201.17) * mm, "end": v(189.07, 201.17) * mm, "construction": true});
            skLineSegment(sketch, "E243", {"start": v(169.07, 153.17) * mm, "end": v(189.07, 153.17) * mm, "construction": true});
            skLineSegment(sketch, "E244", {"start": v(189.07, 163.17) * mm, "end": v(169.07, 163.17) * mm, "construction": true});
            skCircle(sketch, "E245", {"center": v(169.07, 163.17) * mm, "radius": 2.25 * mm});
            skCircle(sketch, "E246", {"center": v(169.07, 153.17) * mm, "radius": 2.25 * mm});
            skCircle(sketch, "E247", {"center": v(189.07, 153.17) * mm, "radius": 2.25 * mm});
            skCircle(sketch, "E248", {"center": v(189.07, 163.17) * mm, "radius": 2.25 * mm});
            skCircle(sketch, "E249", {"center": v(169.07, 211.17) * mm, "radius": 2.25 * mm});
            skCircle(sketch, "E250", {"center": v(169.07, 201.17) * mm, "radius": 2.25 * mm});
            skCircle(sketch, "E251", {"center": v(189.07, 211.17) * mm, "radius": 2.25 * mm});
            skCircle(sketch, "E252", {"center": v(189.07, 201.17) * mm, "radius": 2.25 * mm});
            skCircle(sketch, "E253", {"center": v(179.07, 211.17) * mm, "radius": 2.25 * mm});
            skCircle(sketch, "E254", {"center": v(179.07, 201.17) * mm, "radius": 2.25 * mm});
            skCircle(sketch, "E255", {"center": v(179.07, 153.17) * mm, "radius": 2.25 * mm});
            skCircle(sketch, "E256", {"center": v(179.07, 163.17) * mm, "radius": 2.25 * mm});
            skPoint(sketch, "E257.visualSharp", {"position": v(126.77, 221.17) * mm});
            skPoint(sketch, "E258.visualSharp", {"position": v(231.37, 221.17) * mm});
            skPoint(sketch, "E259.visualSharp", {"position": v(231.37, 143.17) * mm});
            skArc(sketch, "E259.filletArc", {"start": v(221.37, 143.17) * mm, "mid": v(228.44, 146.1) * mm, "end": v(231.37, 153.17) * mm});
            skPoint(sketch, "E260.visualSharp", {"position": v(126.77, 143.17) * mm});
            skArc(sketch, "E260.filletArc", {"start": v(126.77, 153.17) * mm, "mid": v(129.7, 146.1) * mm, "end": v(136.77, 143.17) * mm});
            skCircle(sketch, "E261", {"center": v(136.77, 171.17) * mm, "radius": 3.5 * mm});
            skCircle(sketch, "E262", {"center": v(136.77, 153.17) * mm, "radius": 3.5 * mm});
            skCircle(sketch, "E263", {"center": v(160.77, 171.17) * mm, "radius": 3.5 * mm});
            skCircle(sketch, "E264", {"center": v(160.77, 153.17) * mm, "radius": 3.5 * mm});
            skCircle(sketch, "E265", {"center": v(197.37, 171.17) * mm, "radius": 3.5 * mm});
            skCircle(sketch, "E266", {"center": v(197.37, 153.17) * mm, "radius": 3.5 * mm});
            skCircle(sketch, "E267", {"center": v(221.37, 153.17) * mm, "radius": 3.5 * mm});
            skCircle(sketch, "E268", {"center": v(221.37, 171.17) * mm, "radius": 3.5 * mm});
            skLineSegment(sketch, "E269", {"start": v(169.07, 191.17) * mm, "end": v(189.07, 191.17) * mm});
            skCircle(sketch, "E270", {"center": v(169.07, 191.17) * mm, "radius": 2.25 * mm});
            skCircle(sketch, "E271", {"center": v(179.07, 191.17) * mm, "radius": 2.25 * mm});
            skCircle(sketch, "E272", {"center": v(189.07, 191.17) * mm, "radius": 2.25 * mm});
            skLineSegment(sketch, "E273", {"start": v(159.07, 211.17) * mm, "end": v(159.07, 191.17) * mm});
            skLineSegment(sketch, "E274", {"start": v(149.07, 181.17) * mm, "end": v(136.77, 181.17) * mm});
            skLineSegment(sketch, "E275", {"start": v(199.07, 211.17) * mm, "end": v(199.07, 191.17) * mm});
            skLineSegment(sketch, "E276", {"start": v(209.07, 181.17) * mm, "end": v(221.37, 181.17) * mm});
            skPoint(sketch, "E277.visualSharp", {"position": v(159.07, 221.17) * mm});
            skArc(sketch, "E277.filletArc", {"start": v(169.07, 221.17) * mm, "mid": v(162, 218.24) * mm, "end": v(159.07, 211.17) * mm});
            skPoint(sketch, "E278.visualSharp", {"position": v(199.07, 221.17) * mm});
            skArc(sketch, "E278.filletArc", {"start": v(199.07, 211.17) * mm, "mid": v(196.14, 218.24) * mm, "end": v(189.07, 221.17) * mm});
            skPoint(sketch, "E279.visualSharp", {"position": v(126.77, 181.17) * mm});
            skArc(sketch, "E279.filletArc", {"start": v(136.77, 181.17) * mm, "mid": v(129.7, 178.24) * mm, "end": v(126.77, 171.17) * mm});
            skPoint(sketch, "E280.visualSharp", {"position": v(159.07, 181.17) * mm});
            skArc(sketch, "E280.filletArc", {"start": v(149.07, 181.17) * mm, "mid": v(156.14, 184.1) * mm, "end": v(159.07, 191.17) * mm});
            skPoint(sketch, "E281.visualSharp", {"position": v(199.07, 181.17) * mm});
            skArc(sketch, "E281.filletArc", {"start": v(199.07, 191.17) * mm, "mid": v(202, 184.1) * mm, "end": v(209.07, 181.17) * mm});
            skPoint(sketch, "E282.visualSharp", {"position": v(231.37, 181.17) * mm});
            skArc(sketch, "E282.filletArc", {"start": v(231.37, 171.17) * mm, "mid": v(228.44, 178.24) * mm, "end": v(221.37, 181.17) * mm});
            skSolve(sketch);
        }
        {
            var Q0;
            Q0=makeQuery(id+"F12.imprint","IMPRINT",FACE,{"disambiguationData":[TD([[makeQuery(id+"F12.imprint","IMPRINT",EDGE,{"derivedFrom":sQuery(id+"F12.wireOp",EDGE,"E235")}),-1.0]])]});
            var Q1;
            Q1=makeQuery(id+"F12.imprint","IMPRINT",FACE,{"disambiguationData":[TD([[makeQuery(id+"F12.imprint","IMPRINT",EDGE,{"derivedFrom":sQuery(id+"F12.wireOp",EDGE,"E234")}),-1.0]])]});
            var Q2;
            Q2=makeQuery(id+"F12.imprint","IMPRINT",FACE,{"disambiguationData":[TD([[makeQuery(id+"F12.imprint","IMPRINT",EDGE,{"derivedFrom":sQuery(id+"F12.wireOp",EDGE,"E220")}),-1.0]])]});
            var Q3;
            Q3=makeQuery(id+"F12.imprint","IMPRINT",FACE,{"disambiguationData":[TD([[makeQuery(id+"F12.imprint","IMPRINT",EDGE,{"derivedFrom":sQuery(id+"F12.wireOp",EDGE,"E221")}),-1.0]])]});
            var Q4;
            Q4=makeQuery(id+"F12.imprint","IMPRINT",FACE,{"disambiguationData":[TD([[makeQuery(id+"F12.imprint","IMPRINT",EDGE,{"derivedFrom":sQuery(id+"F12.wireOp",EDGE,"E222")}),-1.0]])]});
            var Q5;
            Q5=makeQuery(id+"F12.imprint","IMPRINT",FACE,{"disambiguationData":[TD([[makeQuery(id+"F12.imprint","IMPRINT",EDGE,{"derivedFrom":sQuery(id+"F12.wireOp",EDGE,"E223")}),-1.0]])]});
            var Q6;
            Q6=makeQuery(id+"F12.imprint","IMPRINT",FACE,{"disambiguationData":[TD([[makeQuery(id+"F12.imprint","IMPRINT",EDGE,{"derivedFrom":sQuery(id+"F12.wireOp",EDGE,"E225")}),-1.0]])]});
            var Q7;
            Q7=makeQuery(id+"F12.imprint","IMPRINT",FACE,{"disambiguationData":[TD([[makeQuery(id+"F12.imprint","IMPRINT",EDGE,{"derivedFrom":sQuery(id+"F12.wireOp",EDGE,"E224")}),-1.0]])]});
            var Q8;
            Q8=makeQuery(id+"F12.imprint","IMPRINT",FACE,{"disambiguationData":[TD([[makeQuery(id+"F12.imprint","IMPRINT",EDGE,{"derivedFrom":sQuery(id+"F12.wireOp",EDGE,"E226")}),-1.0]])]});
            var Q9;
            Q9=makeQuery(id+"F12.imprint","IMPRINT",FACE,{"disambiguationData":[TD([[makeQuery(id+"F12.imprint","IMPRINT",EDGE,{"derivedFrom":sQuery(id+"F12.wireOp",EDGE,"E219.top")}),-1.0]])]});
            var Q10;
            Q10=makeQuery(id+"F12.imprint","IMPRINT",FACE,{"disambiguationData":[TD([[makeQuery(id+"F12.imprint","IMPRINT",EDGE,{"derivedFrom":sQuery(id+"F12.wireOp",EDGE,"E227")}),-1.0]])]});
            extrude(context, id + "F13", {"entities" : qUnion([Q0, Q1, Q2, Q3, Q4, Q5, Q6, Q7, Q8, Q9, Q10]), "oppositeDirection" : true, "depth" : 12.7 * mm});
        }
        {
            var Q0;
            Q0=makeQuery(id+"F12.imprint","IMPRINT",FACE,{"disambiguationData":[TD([[makeQuery(id+"F12.imprint","IMPRINT",EDGE,{"derivedFrom":sQuery(id+"F12.wireOp",EDGE,"E222")}),-1.0]])]});
            var Q1;
            Q1=makeQuery(id+"F12.imprint","IMPRINT",FACE,{"disambiguationData":[TD([[makeQuery(id+"F12.imprint","IMPRINT",EDGE,{"derivedFrom":sQuery(id+"F12.wireOp",EDGE,"E220")}),-1.0]])]});
            var Q2;
            Q2=makeQuery(id+"F12.imprint","IMPRINT",FACE,{"disambiguationData":[TD([[makeQuery(id+"F12.imprint","IMPRINT",EDGE,{"derivedFrom":sQuery(id+"F12.wireOp",EDGE,"E221")}),-1.0]])]});
            var Q3;
            Q3=makeQuery(id+"F12.imprint","IMPRINT",FACE,{"disambiguationData":[TD([[makeQuery(id+"F12.imprint","IMPRINT",EDGE,{"derivedFrom":sQuery(id+"F12.wireOp",EDGE,"E223")}),-1.0]])]});
            var Q4;
            Q4=makeQuery(id+"F12.imprint","IMPRINT",FACE,{"disambiguationData":[TD([[makeQuery(id+"F12.imprint","IMPRINT",EDGE,{"derivedFrom":sQuery(id+"F12.wireOp",EDGE,"E235")}),-1.0]])]});
            var Q5;
            Q5=makeQuery(id+"F12.imprint","IMPRINT",FACE,{"disambiguationData":[TD([[makeQuery(id+"F12.imprint","IMPRINT",EDGE,{"derivedFrom":sQuery(id+"F12.wireOp",EDGE,"E234")}),-1.0]])]});
            var Q6;
            Q6=makeQuery(id+"F12.imprint","IMPRINT",FACE,{"disambiguationData":[TD([[makeQuery(id+"F12.imprint","IMPRINT",EDGE,{"derivedFrom":sQuery(id+"F12.wireOp",EDGE,"E225")}),-1.0]])]});
            var Q7;
            Q7=makeQuery(id+"F12.imprint","IMPRINT",FACE,{"disambiguationData":[TD([[makeQuery(id+"F12.imprint","IMPRINT",EDGE,{"derivedFrom":sQuery(id+"F12.wireOp",EDGE,"E226")}),-1.0]])]});
            var Q8;
            Q8=makeQuery(id+"F12.imprint","IMPRINT",FACE,{"disambiguationData":[TD([[makeQuery(id+"F12.imprint","IMPRINT",EDGE,{"derivedFrom":sQuery(id+"F12.wireOp",EDGE,"E227")}),-1.0]])]});
            var Q9;
            Q9=makeQuery(id+"F12.imprint","IMPRINT",FACE,{"disambiguationData":[TD([[makeQuery(id+"F12.imprint","IMPRINT",EDGE,{"derivedFrom":sQuery(id+"F12.wireOp",EDGE,"E224")}),-1.0]])]});
            extrude(context, id + "F14", {"entities" : qUnion([Q0, Q1, Q2, Q3, Q4, Q5, Q6, Q7, Q8, Q9]), "operationType" : NewBodyOperationType.REMOVE, "oppositeDirection" : true, "depth" : 5 * mm});
        }
        {
            var Q0;
            Q0=qCreatedBy(makeId("Top.planeOp"),FACE);
            var sketch = newSketch(context, id + "F15", { "sketchPlane" : qUnion([Q0])});
            skLineSegment(sketch, "E283.bottom", {"start": v(-29.57, 84.03) * mm, "end": v(-3.57, 84.03) * mm});
            skLineSegment(sketch, "E283.top", {"start": v(-29.57, 71.33) * mm, "end": v(-3.57, 71.33) * mm});
            skLineSegment(sketch, "E283.left", {"start": v(-29.57, 84.03) * mm, "end": v(-29.57, 71.33) * mm});
            skLineSegment(sketch, "E283.right", {"start": v(-3.57, 84.03) * mm, "end": v(-3.57, 71.33) * mm});
            skPoint(sketch, "E284.0", {"position": v(171.07, 170.82) * mm});
            skPoint(sketch, "E284.1", {"position": v(187.07, 170.82) * mm});
            skLineSegment(sketch, "E285", {"start": v(171.07, 170.82) * mm, "end": v(187.07, 170.82) * mm, "construction": true});
            skLineSegment(sketch, "E286", {"start": v(-24.57, 77.68) * mm, "end": v(-8.57, 77.68) * mm, "construction": true});
            skLineSegment(sketch, "E287", {"start": v(-24.57, 77.68) * mm, "end": v(-29.57, 77.68) * mm, "construction": true});
            skPoint(sketch, "E288.endSnap0", {"position": v(-3.57, 77.68) * mm});
            skLineSegment(sketch, "E289", {"start": v(-8.57, 77.68) * mm, "end": v(-3.57, 77.68) * mm, "construction": true});
            skCircle(sketch, "E290", {"center": v(-24.57, 77.68) * mm, "radius": 2.25 * mm});
            skCircle(sketch, "E291", {"center": v(-8.57, 77.68) * mm, "radius": 2.25 * mm});
            skLineSegment(sketch, "E292", {"start": v(-29.57, 96.73) * mm, "end": v(-3.57, 96.73) * mm});
            skLineSegment(sketch, "E293", {"start": v(-3.57, 96.73) * mm, "end": v(-3.57, 84.03) * mm});
            skLineSegment(sketch, "E294", {"start": v(-29.57, 84.03) * mm, "end": v(-29.57, 96.73) * mm});
            skLineSegment(sketch, "E295", {"start": v(-29.57, 71.33) * mm, "end": v(-29.57, 58.63) * mm});
            skLineSegment(sketch, "E296", {"start": v(-29.57, 58.63) * mm, "end": v(-3.57, 58.63) * mm});
            skLineSegment(sketch, "E297", {"start": v(-3.57, 58.63) * mm, "end": v(-3.57, 71.33) * mm});
            skSolve(sketch);
        }
        {
            var Q0;
            Q0=makeQuery(id+"F15.imprint","IMPRINT",FACE,{"disambiguationData":[TD([[makeQuery(id+"F15.imprint","IMPRINT",EDGE,{"derivedFrom":sQuery(id+"F15.wireOp",EDGE,"E283.bottom")}),1.0]])]});
            var Q1;
            Q1=makeQuery(id+"F15.imprint","IMPRINT",FACE,{"disambiguationData":[TD([[makeQuery(id+"F15.imprint","IMPRINT",EDGE,{"derivedFrom":sQuery(id+"F15.wireOp",EDGE,"E283.bottom")}),-1.0]])]});
            var Q2;
            Q2=makeQuery(id+"F15.imprint","IMPRINT",FACE,{"disambiguationData":[TD([[makeQuery(id+"F15.imprint","IMPRINT",EDGE,{"derivedFrom":sQuery(id+"F15.wireOp",EDGE,"E283.top")}),-1.0]])]});
            extrude(context, id + "F16", {"entities" : qUnion([Q0, Q1, Q2]), "oppositeDirection" : true, "depth" : 1 / 50.8 * mm});
        }
        {
            var Q0;
            Q0=makeQuery(id+"F15.imprint","IMPRINT",FACE,{"disambiguationData":[TD([[makeQuery(id+"F15.imprint","IMPRINT",EDGE,{"derivedFrom":sQuery(id+"F15.wireOp",EDGE,"E283.bottom")}),-1.0]])]});
            extrude(context, id + "F17", {"entities" : qUnion([Q0]), "operationType" : NewBodyOperationType.REMOVE, "oppositeDirection" : true, "depth" : 1 / 101.6 * mm});
        }
        {
            var Q0;
            Q0=qCreatedBy(makeId("Top.planeOp"),FACE);
            var sketch = newSketch(context, id + "F18", { "sketchPlane" : qUnion([Q0])});
            skPoint(sketch, "E298.0", {"position": v(-24.57, 77.68) * mm});
            skPoint(sketch, "E298.1", {"position": v(-8.57, 77.68) * mm});
            skLineSegment(sketch, "E299", {"start": v(-24.57, 77.68) * mm, "end": v(-24.57, 106.73) * mm, "construction": true});
            skLineSegment(sketch, "E300", {"start": v(-8.57, 77.68) * mm, "end": v(-8.57, 106.73) * mm, "construction": true});
            skPoint(sketch, "E301.0", {"position": v(-29.57, 96.73) * mm});
            skPoint(sketch, "E301.1", {"position": v(-3.57, 96.73) * mm});
            skLineSegment(sketch, "E302", {"start": v(-29.57, 96.73) * mm, "end": v(-29.57, 106.73) * mm, "construction": true});
            skLineSegment(sketch, "E303", {"start": v(-29.57, 106.73) * mm, "end": v(-3.57, 106.73) * mm});
            skLineSegment(sketch, "E304", {"start": v(-3.57, 106.73) * mm, "end": v(-3.57, 96.73) * mm, "construction": true});
            skLineSegment(sketch, "E305", {"start": v(-29.57, 106.73) * mm, "end": v(-29.57, 139.98) * mm});
            skLineSegment(sketch, "E306", {"start": v(-29.57, 139.98) * mm, "end": v(-3.57, 139.98) * mm});
            skLineSegment(sketch, "E307", {"start": v(-3.57, 139.98) * mm, "end": v(-3.57, 106.73) * mm});
            skLineSegment(sketch, "E308", {"start": v(-16.57, 139.98) * mm, "end": v(-16.57, 106.73) * mm, "construction": true});
            skCircle(sketch, "E309", {"center": v(-16.57, 127.98) * mm, "radius": 6.25 * mm});
            skPoint(sketch, "E310", {"position": v(-16.57, 121.73) * mm});
            skLineSegment(sketch, "E311", {"start": v(-25.07, 117.98) * mm, "end": v(-8.07, 117.98) * mm});
            skPoint(sketch, "E312", {"position": v(-16.57, 117.98) * mm});
            skLineSegment(sketch, "E313", {"start": v(-25.07, 117.98) * mm, "end": v(-25.07, 139.98) * mm});
            skLineSegment(sketch, "E314", {"start": v(-8.07, 117.98) * mm, "end": v(-8.07, 139.98) * mm});
            skSolve(sketch);
        }
        {
            var Q0;
            Q0=makeQuery(id+"F18.imprint","IMPRINT",FACE,{"disambiguationData":[TD([[makeQuery(id+"F18.imprint","IMPRINT",EDGE,{"derivedFrom":sQuery(id+"F18.wireOp",EDGE,"E309")}),-1.0]])]});
            var Q1;
            Q1=makeQuery(id+"F18.imprint","IMPRINT",FACE,{"disambiguationData":[TD([[makeQuery(id+"F18.imprint","IMPRINT",EDGE,{"derivedFrom":sQuery(id+"F18.wireOp",EDGE,"E303")}),1.0]])]});
            extrude(context, id + "F19", {"entities" : qUnion([Q0, Q1]), "oppositeDirection" : true, "depth" : 1 / 50.8 * mm});
        }
        {
            var Q0;
            Q0=makeQuery(id+"F18.imprint","IMPRINT",FACE,{"disambiguationData":[TD([[makeQuery(id+"F18.imprint","IMPRINT",EDGE,{"derivedFrom":sQuery(id+"F18.wireOp",EDGE,"E309")}),-1.0]])]});
            extrude(context, id + "F20", {"entities" : qUnion([Q0]), "operationType" : NewBodyOperationType.REMOVE, "oppositeDirection" : true, "depth" : 6 * mm});
        }
    });
